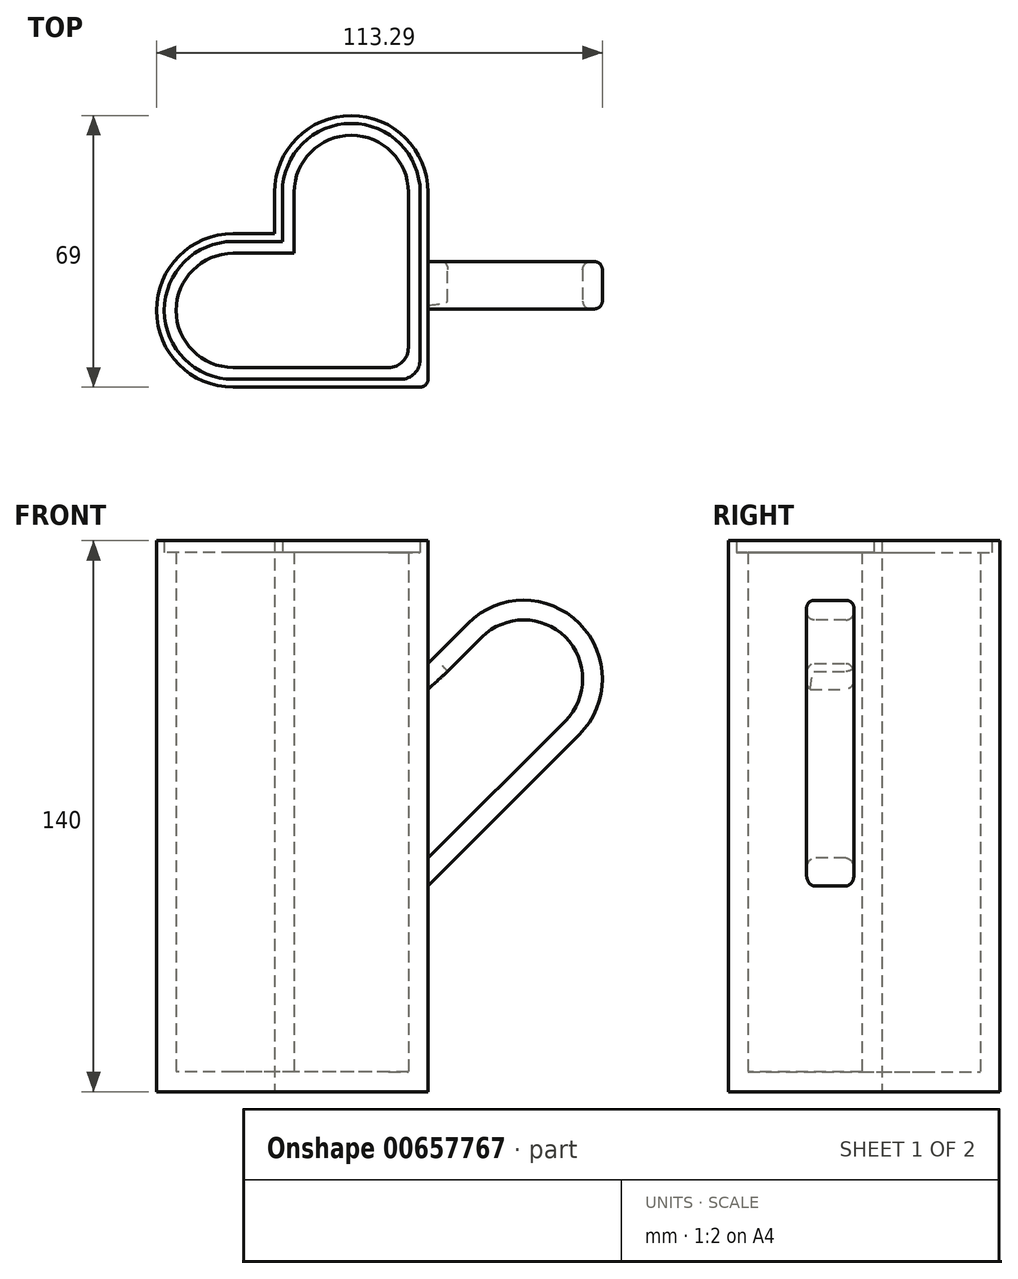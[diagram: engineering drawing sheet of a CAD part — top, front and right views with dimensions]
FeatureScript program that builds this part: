
annotation { "Feature Type Name" : "Feature", "Feature Type Description" : "" }
export const myFeature = defineFeature(function(context is Context, id is Id, definition is map)
    precondition{}
    {
        {
            var Q0;
            Q0=qCreatedBy(makeId("Top.planeOp"),FACE);
            var sketch = newSketch(context, id + "F0", { "sketchPlane" : qUnion([Q0])});
            skLineSegment(sketch, "E0", {"start": v(0, 0) * mm, "end": v(0, 47.5) * mm});
            skLineSegment(sketch, "E1", {"start": v(0, 0) * mm, "end": v(-47.5, 0) * mm});
            skLineSegment(sketch, "E2", {"start": v(-35, 35) * mm, "end": v(-47.5, 35) * mm});
            skLineSegment(sketch, "E3", {"start": v(-35, 35) * mm, "end": v(-35, 47.5) * mm});
            skArc(sketch, "E4", {"start": v(-47.5, 35) * mm, "mid": v(-65, 17.5) * mm, "end": v(-47.5, 0) * mm});
            skArc(sketch, "E5", {"start": v(-35, 47.5) * mm, "mid": v(-17.5, 65) * mm, "end": v(0, 47.5) * mm});
            skLineSegment(sketch, "E6.0", {"start": v(-37, 37) * mm, "end": v(-37, 47.5) * mm});
            skArc(sketch, "E6.1", {"start": v(-47.5, 37) * mm, "mid": v(-67, 17.5) * mm, "end": v(-47.5, -2) * mm});
            skLineSegment(sketch, "E6.2", {"start": v(2, -2) * mm, "end": v(-47.5, -2) * mm});
            skLineSegment(sketch, "E6.3", {"start": v(-37, 37) * mm, "end": v(-47.5, 37) * mm});
            skLineSegment(sketch, "E6.4", {"start": v(2, -2) * mm, "end": v(2, 47.5) * mm});
            skArc(sketch, "E6.5", {"start": v(-37, 47.5) * mm, "mid": v(-17.5, 67) * mm, "end": v(2, 47.5) * mm});
            skLineSegment(sketch, "E7.0", {"start": v(-32, 32) * mm, "end": v(-47.5, 32) * mm});
            skArc(sketch, "E7.1", {"start": v(-32, 47.5) * mm, "mid": v(-17.5, 62) * mm, "end": v(-3, 47.5) * mm});
            skLineSegment(sketch, "E7.2", {"start": v(-3, 3) * mm, "end": v(-3, 47.5) * mm});
            skLineSegment(sketch, "E7.3", {"start": v(-32, 32) * mm, "end": v(-32, 47.5) * mm});
            skLineSegment(sketch, "E7.4", {"start": v(-3, 3) * mm, "end": v(-47.5, 3) * mm});
            skArc(sketch, "E7.5", {"start": v(-47.5, 32) * mm, "mid": v(-62, 17.5) * mm, "end": v(-47.5, 3) * mm});
            skSolve(sketch);
        }
        {
            var Q0;
            Q0 = qSketchRegion(id + "F0", true);
            extrude(context, id + "F1", {"entities" : qUnion([Q0]), "depth" : 140 * mm, "offsetDistance" : 25 * mm});
        }
        {
            var Q0;
            Q0=makeQuery(id+"F0.imprint","IMPRINT",FACE,{"disambiguationData":[TD([[makeQuery(id+"F0.imprint","IMPRINT",EDGE,{"derivedFrom":sQuery(id+"F0.wireOp",EDGE,"E0")}),1.0]])]});
            extrude(context, id + "F2", {"entities" : qUnion([Q0]), "operationType" : NewBodyOperationType.ADD, "depth" : 137 * mm, "offsetDistance" : 25 * mm});
        }
        {
            var Q0;
            Q0=makeQuery(id+"F0.imprint","IMPRINT",FACE,{"disambiguationData":[TD([[makeQuery(id+"F0.imprint","IMPRINT",EDGE,{"derivedFrom":sQuery(id+"F0.wireOp",EDGE,"E7.0")}),1.0]])]});
            extrude(context, id + "F3", {"entities" : qUnion([Q0]), "operationType" : NewBodyOperationType.ADD, "depth" : 5 * mm, "offsetDistance" : 25 * mm});
        }
        {
            var Q0;
            Q0=makeQuery(id+"F1.opExtrude","SWEPT_FACE",FACE,{"disambiguationData":[OSD([sQuery(id+"F0.wireOp",EDGE,"E6.4")])]});
            var sketch = newSketch(context, id + "F4", { "sketchPlane" : qUnion([Q0])});
            skLineSegment(sketch, "E8.bottom", {"start": v(17.89, 108.85) * mm, "end": v(21.94, 108.85) * mm});
            skLineSegment(sketch, "E8.top", {"start": v(17.89, 102.23) * mm, "end": v(21.94, 102.23) * mm});
            skLineSegment(sketch, "E8.left", {"start": v(17.89, 108.85) * mm, "end": v(17.89, 102.23) * mm});
            skLineSegment(sketch, "E8.right", {"start": v(21.94, 108.85) * mm, "end": v(21.94, 102.23) * mm});
            skSolve(sketch);
        }
        {
            var Q0;
            Q0 = qSketchRegion(id + "F4", true);
            extrude(context, id + "F5", {"entities" : qUnion([Q0]), "operationType" : NewBodyOperationType.ADD, "depth" : 5 * mm, "offsetDistance" : 25 * mm});
        }
        {
            var Q0;
            Q0=makeQuery(id+"F5.opExtrude","SWEPT_FACE",FACE,{"disambiguationData":[OSD([sQuery(id+"F4.wireOp",EDGE,"E8.left")])]});
            var sketch = newSketch(context, id + "F6", { "sketchPlane" : qUnion([Q0])});
            skLineSegment(sketch, "E9", {"start": v(2, 108.85) * mm, "end": v(12.15, 119) * mm});
            skLineSegment(sketch, "E10", {"start": v(2, 52.28) * mm, "end": v(40.43, 90.71) * mm});
            skLineSegment(sketch, "E11", {"start": v(12.15, 119) * mm, "end": v(44.67, 86.47) * mm, "construction": true});
            skArc(sketch, "E12", {"start": v(12.15, 119) * mm, "mid": v(40.43, 119) * mm, "end": v(40.43, 90.71) * mm});
            skLineSegment(sketch, "E13.0", {"start": v(-1.54, 55.81) * mm, "end": v(36.9, 94.25) * mm});
            skArc(sketch, "E13.1", {"start": v(15.68, 115.46) * mm, "mid": v(36.9, 115.46) * mm, "end": v(36.9, 94.25) * mm});
            skLineSegment(sketch, "E13.2", {"start": v(5.54, 105.31) * mm, "end": v(15.68, 115.46) * mm});
            skLineSegment(sketch, "E14", {"start": v(5.54, 105.31) * mm, "end": v(2, 102.23) * mm});
            skLineSegment(sketch, "E15", {"start": v(2, 102.23) * mm, "end": v(2, 108.85) * mm});
            skLineSegment(sketch, "E16", {"start": v(2, 52.28) * mm, "end": v(2, 59.35) * mm});
            skSolve(sketch);
        }
        {
            var Q0;
            Q0 = qSketchRegion(id + "F6", true);
            extrude(context, id + "F7", {"entities" : qUnion([Q0]), "operationType" : NewBodyOperationType.ADD, "oppositeDirection" : true, "depth" : 12 * mm, "offsetDistance" : 25 * mm});
        }
        {
            var Q0;
            Q0=makeQuery(id+"F7.boolean.opBoolean","MERGE",FACE,{"derivedFrom":[makeQuery(id+"F5.opExtrude","SWEPT_FACE",FACE,{"disambiguationData":[OSD([sQuery(id+"F4.wireOp",EDGE,"E8.left")])]}),makeQuery(id+"F7.opExtrude","CAP_FACE",FACE,{"disambiguationData":[OSD([sQuery(id+"F6.wireOp",EDGE,"E9"),sQuery(id+"F6.wireOp",EDGE,"E10"),sQuery(id+"F6.wireOp",EDGE,"E12"),sQuery(id+"F6.wireOp",EDGE,"E13.0"),sQuery(id+"F6.wireOp",EDGE,"E13.1"),sQuery(id+"F6.wireOp",EDGE,"E13.2"),sQuery(id+"F6.wireOp",EDGE,"E14"),sQuery(id+"F6.wireOp",EDGE,"E15"),sQuery(id+"F6.wireOp",EDGE,"E16")])],"isStart":true})]});
            var sketch = newSketch(context, id + "F8", { "sketchPlane" : qUnion([Q0])});
            skLineSegment(sketch, "E17", {"start": v(7, 106.78) * mm, "end": v(2, 102.23) * mm});
            skSolve(sketch);
        }
        {
            var Q0;
            Q0=makeQuery(id+"F8.imprint","IMPRINT",FACE,{"disambiguationData":[TD([[makeQuery(id+"F8.imprint","IMPRINT",EDGE,{"derivedFrom":sQuery(id+"F8.wireOp",EDGE,"E17")}),1.0]])]});
            extrude(context, id + "F9", {"entities" : qUnion([Q0]), "operationType" : NewBodyOperationType.REMOVE, "oppositeDirection" : true, "depth" : 31 * mm, "offsetDistance" : 25 * mm});
        }
        {
            var Q0;
            Q0=makeQuery(id+"F3.opExtrude","CAP_EDGE",EDGE,{"disambiguationData":[OSD([sQuery(id+"F0.wireOp",EDGE,"E7.5")])],"isStart":false});
            var Q1;
            Q1=makeQuery(id+"F3.opExtrude","CAP_EDGE",EDGE,{"disambiguationData":[OSD([sQuery(id+"F0.wireOp",EDGE,"E7.3")])],"isStart":false});
            var Q2;
            Q2=makeQuery(id+"F2.opExtrude","SWEPT_EDGE",EDGE,{"disambiguationData":[OSD([sQuery(id+"F0.wireOp",EDGE,"E7.2"),sQuery(id+"F0.wireOp",EDGE,"E7.4")])]});
            fillet(context, id + "F10", {"entities" : qUnion([Q0, Q1, Q2]), "radius" : 5 * mm, "tangentPropagation" : true, "allowEdgeOverflow" : false});
        }
        {
            var Q0;
            Q0=makeQuery(id+"F7.opExtrude","CAP_EDGE",EDGE,{"disambiguationData":[OSD([sQuery(id+"F6.wireOp",EDGE,"E12")])],"isStart":true});
            var Q1;
            Q1=makeQuery(id+"F7.opExtrude","CAP_EDGE",EDGE,{"disambiguationData":[OSD([sQuery(id+"F6.wireOp",EDGE,"E9")])],"isStart":true});
            var Q2;
            Q2=makeQuery(id+"F7.opExtrude","CAP_EDGE",EDGE,{"disambiguationData":[OSD([sQuery(id+"F6.wireOp",EDGE,"E10")])],"isStart":true});
            var Q3;
            Q3=makeQuery(id+"F7.opExtrude","CAP_EDGE",EDGE,{"disambiguationData":[OSD([sQuery(id+"F6.wireOp",EDGE,"E13.1")])],"isStart":true});
            var Q4;
            Q4=makeQuery(id+"F7.opExtrude","CAP_EDGE",EDGE,{"disambiguationData":[OSD([sQuery(id+"F6.wireOp",EDGE,"E13.2")])],"isStart":true});
            var Q5;
            Q5=makeQuery(id+"F9.boolean.opBoolean","COPY",EDGE,{"derivedFrom":makeQuery(id+"F9.opExtrude","CAP_EDGE",EDGE,{"disambiguationData":[OSD([sQuery(id+"F8.wireOp",EDGE,"E17")])],"isStart":true})});
            var Q6;
            Q6=makeQuery(id+"F7.opExtrude","CAP_EDGE",EDGE,{"disambiguationData":[OSD([sQuery(id+"F6.wireOp",EDGE,"E13.0")])],"isStart":true});
            var Q7;
            Q7=makeQuery(id+"F7.opExtrude","CAP_EDGE",EDGE,{"disambiguationData":[OSD([sQuery(id+"F6.wireOp",EDGE,"E10")])],"isStart":false});
            var Q8;
            Q8=makeQuery(id+"F7.opExtrude","CAP_EDGE",EDGE,{"disambiguationData":[OSD([sQuery(id+"F6.wireOp",EDGE,"E12")])],"isStart":false});
            var Q9;
            Q9=makeQuery(id+"F7.opExtrude","CAP_EDGE",EDGE,{"disambiguationData":[OSD([sQuery(id+"F6.wireOp",EDGE,"E13.0")])],"isStart":false});
            var Q10;
            Q10=makeQuery(id+"F7.opExtrude","CAP_EDGE",EDGE,{"disambiguationData":[OSD([sQuery(id+"F6.wireOp",EDGE,"E13.1")])],"isStart":false});
            var Q11;
            Q11=makeQuery(id+"F7.opExtrude","CAP_EDGE",EDGE,{"disambiguationData":[OSD([sQuery(id+"F6.wireOp",EDGE,"E13.2")])],"isStart":false});
            var Q12;
            Q12=makeQuery(id+"F9.boolean.opBoolean","INTERSECT",EDGE,{"derivedFrom":[makeQuery(id+"F7.opExtrude","CAP_FACE",FACE,{"disambiguationData":[OSD([sQuery(id+"F6.wireOp",EDGE,"E9"),sQuery(id+"F6.wireOp",EDGE,"E10"),sQuery(id+"F6.wireOp",EDGE,"E12"),sQuery(id+"F6.wireOp",EDGE,"E13.0"),sQuery(id+"F6.wireOp",EDGE,"E13.1"),sQuery(id+"F6.wireOp",EDGE,"E13.2"),sQuery(id+"F6.wireOp",EDGE,"E14"),sQuery(id+"F6.wireOp",EDGE,"E15"),sQuery(id+"F6.wireOp",EDGE,"E16")])],"isStart":false}),makeQuery(id+"F9.opExtrude","SWEPT_FACE",FACE,{"disambiguationData":[OSD([sQuery(id+"F8.wireOp",EDGE,"E17")])]})]});
            var Q13;
            Q13=makeQuery(id+"F7.opExtrude","CAP_EDGE",EDGE,{"disambiguationData":[OSD([sQuery(id+"F6.wireOp",EDGE,"E9")])],"isStart":false});
            fillet(context, id + "F11", {"entities" : qUnion([Q0, Q1, Q2, Q3, Q4, Q5, Q6, Q7, Q8, Q9, Q10, Q11, Q12, Q13]), "radius" : 2 * mm, "tangentPropagation" : true, "allowEdgeOverflow" : false});
        }
        {
            var Q0;
            Q0=makeQuery(id+"F1.opExtrude","SWEPT_EDGE",EDGE,{"disambiguationData":[OSD([sQuery(id+"F0.wireOp",EDGE,"E6.2"),sQuery(id+"F0.wireOp",EDGE,"E6.4")])]});
            fillet(context, id + "F12", {"entities" : qUnion([Q0]), "radius" : 2 * mm, "tangentPropagation" : true, "allowEdgeOverflow" : false});
        }
        {
            var Q0;
            Q0=makeQuery(id+"F1.opExtrude","SWEPT_EDGE",EDGE,{"disambiguationData":[OSD([sQuery(id+"F0.wireOp",EDGE,"E0"),sQuery(id+"F0.wireOp",EDGE,"E1")])]});
            fillet(context, id + "F13", {"entities" : qUnion([Q0]), "radius" : 5 * mm, "tangentPropagation" : true, "allowEdgeOverflow" : false});
        }
    });
